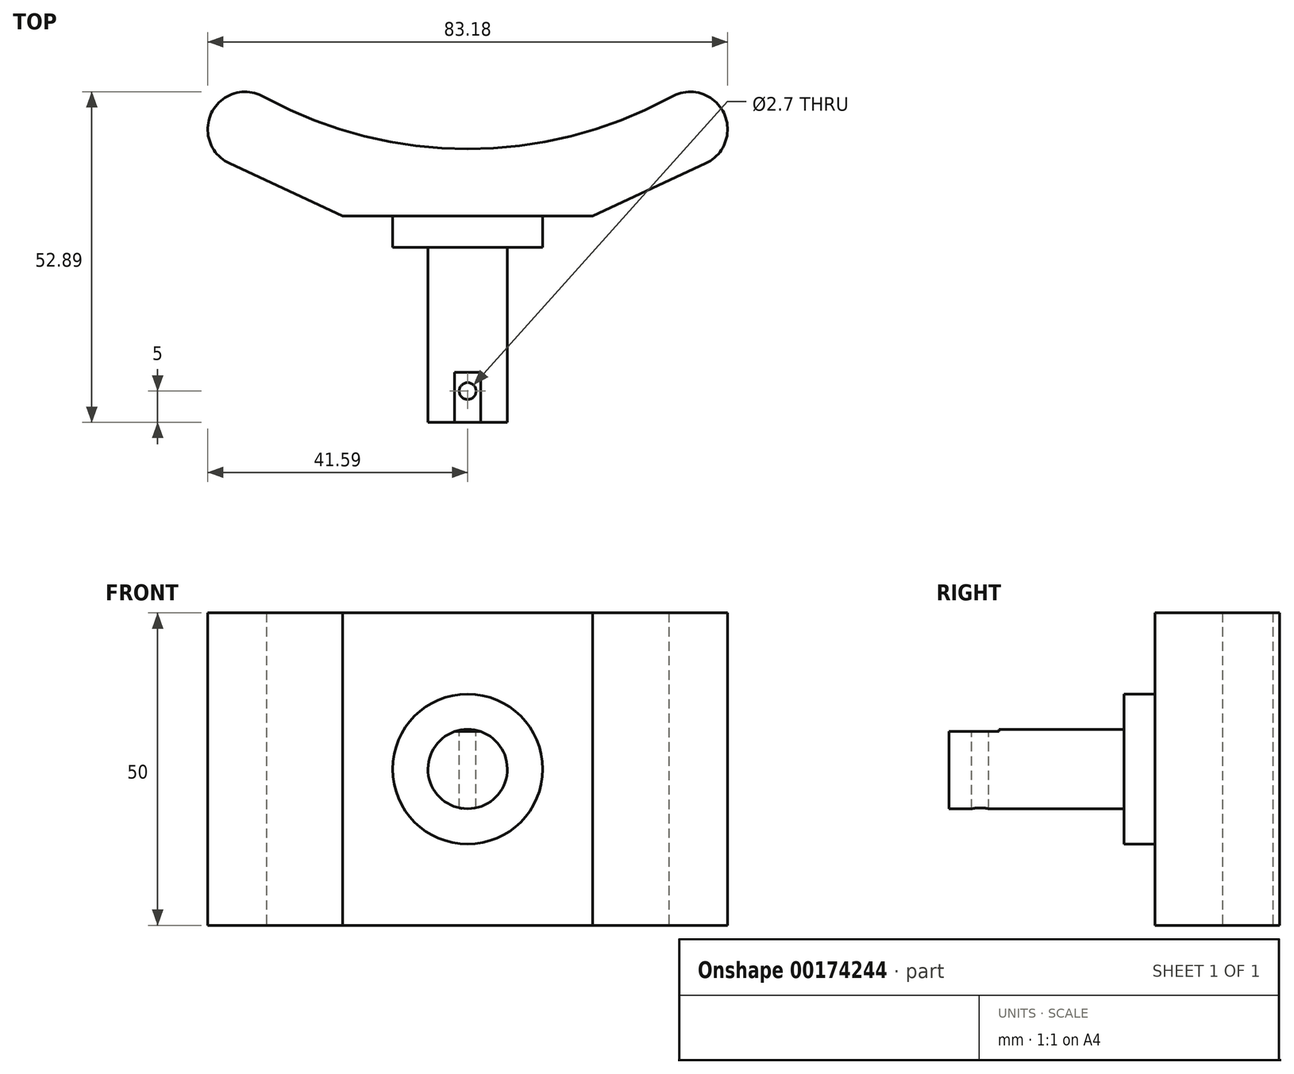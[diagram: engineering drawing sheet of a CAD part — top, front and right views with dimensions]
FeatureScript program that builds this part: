
annotation { "Feature Type Name" : "Feature", "Feature Type Description" : "" }
export const myFeature = defineFeature(function(context is Context, id is Id, definition is map)
    precondition{}
    {
        {
            var Q0;
            Q0=qCreatedBy(makeId("Top.planeOp"),FACE);
            var sketch = newSketch(context, id + "F0", { "sketchPlane" : qUnion([Q0])});
            skLineSegment(sketch, "E0", {"start": v(-20, 0) * mm, "end": v(20, 0) * mm});
            skLineSegment(sketch, "E1", {"start": v(20, 0) * mm, "end": v(38.13, 8.45) * mm});
            skLineSegment(sketch, "E2", {"start": v(-20, 0) * mm, "end": v(-38.13, 8.45) * mm});
            skArc(sketch, "E3", {"start": v(-32.2, 18.85) * mm, "mid": v(-40.8, 16.86) * mm, "end": v(-38.13, 8.45) * mm});
            skArc(sketch, "E4", {"start": v(38.13, 8.45) * mm, "mid": v(40.8, 16.86) * mm, "end": v(32.2, 18.85) * mm});
            skArc(sketch, "E5", {"start": v(-32.2, 18.85) * mm, "mid": v(0, 10.76) * mm, "end": v(32.2, 18.85) * mm});
            skSolve(sketch);
        }
        {
            var Q0;
            Q0 = qSketchRegion(id + "F0", true);
            extrude(context, id + "F1", {"entities" : qUnion([Q0]), "depth" : 50 * mm});
        }
        {
            var Q0;
            Q0=makeQuery(id+"F1.opExtrude","SWEPT_FACE",FACE,{"disambiguationData":[OSD([sQuery(id+"F0.wireOp",EDGE,"E0")])]});
            var sketch = newSketch(context, id + "F2", { "sketchPlane" : qUnion([Q0])});
            skCircle(sketch, "E6", {"center": v(0, 25) * mm, "radius": 12 * mm});
            skPoint(sketch, "E6.centerSnap0", {"position": v(20, 25) * mm});
            skSolve(sketch);
        }
        {
            var Q0;
            Q0 = qSketchRegion(id + "F2", true);
            extrude(context, id + "F3", {"entities" : qUnion([Q0]), "operationType" : NewBodyOperationType.ADD, "depth" : 5 * mm});
        }
        {
            var Q0;
            Q0=makeQuery(id+"F3.opExtrude","CAP_FACE",FACE,{"disambiguationData":[OSD([sQuery(id+"F2.wireOp",EDGE,"E6")])],"isStart":false});
            var sketch = newSketch(context, id + "F4", { "sketchPlane" : qUnion([Q0])});
            skCircle(sketch, "E7", {"center": v(0, 25) * mm, "radius": 6.35 * mm});
            skSolve(sketch);
        }
        {
            var Q0;
            Q0 = qSketchRegion(id + "F4", true);
            extrude(context, id + "F5", {"entities" : qUnion([Q0]), "operationType" : NewBodyOperationType.ADD, "depth" : 28 * mm});
        }
        {
            var Q0;
            Q0=makeQuery(id+"F1.opExtrude","CAP_FACE",FACE,{"disambiguationData":[OSD([sQuery(id+"F0.wireOp",EDGE,"E0"),sQuery(id+"F0.wireOp",EDGE,"E1"),sQuery(id+"F0.wireOp",EDGE,"E2"),sQuery(id+"F0.wireOp",EDGE,"E3"),sQuery(id+"F0.wireOp",EDGE,"E4"),sQuery(id+"F0.wireOp",EDGE,"E5")])],"isStart":false});
            var sketch = newSketch(context, id + "F6", { "sketchPlane" : qUnion([Q0])});
            skLineSegment(sketch, "E8.bottom", {"start": v(-18.1, -25) * mm, "end": v(18.84, -25) * mm});
            skLineSegment(sketch, "E8.top", {"start": v(-18.1, -47.77) * mm, "end": v(18.84, -47.77) * mm});
            skLineSegment(sketch, "E8.left", {"start": v(-18.1, -25) * mm, "end": v(-18.1, -47.77) * mm});
            skLineSegment(sketch, "E8.right", {"start": v(18.84, -25) * mm, "end": v(18.84, -47.77) * mm});
            skSolve(sketch);
        }
        {
            var Q0;
            Q0 = qSketchRegion(id + "F6", true);
            extrude(context, id + "F7", {"entities" : qUnion([Q0]), "operationType" : NewBodyOperationType.REMOVE, "oppositeDirection" : true, "depth" : 19 * mm});
        }
        {
            var Q0;
            Q0=makeQuery(id+"F7.boolean.opBoolean","COPY",FACE,{"derivedFrom":makeQuery(id+"F7.opExtrude","CAP_FACE",FACE,{"disambiguationData":[OSD([sQuery(id+"F6.wireOp",EDGE,"E8.bottom"),sQuery(id+"F6.wireOp",EDGE,"E8.top"),sQuery(id+"F6.wireOp",EDGE,"E8.left"),sQuery(id+"F6.wireOp",EDGE,"E8.right")])],"isStart":false})});
            var sketch = newSketch(context, id + "F8", { "sketchPlane" : qUnion([Q0])});
            skCircle(sketch, "E9", {"center": v(0, -28) * mm, "radius": 1.35 * mm});
            skSolve(sketch);
        }
        {
            var Q0;
            Q0 = qSketchRegion(id + "F8", true);
            extrude(context, id + "F9", {"entities" : qUnion([Q0]), "operationType" : NewBodyOperationType.REMOVE, "endBound" : BoundingType.THROUGH_ALL, "oppositeDirection" : true, "depth" : 25 * mm});
        }
    });
